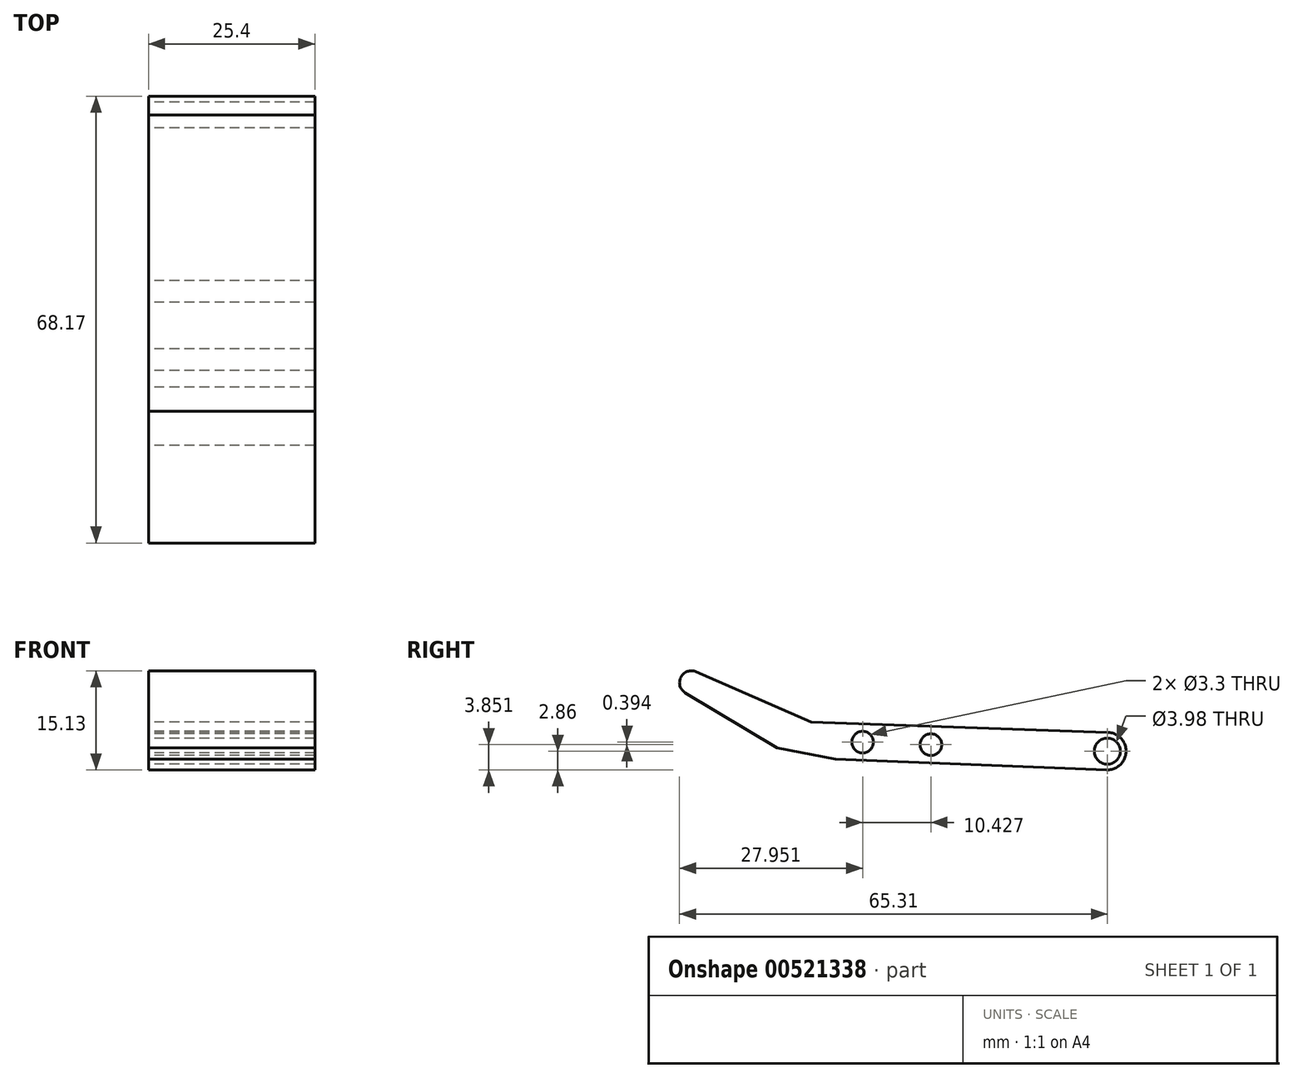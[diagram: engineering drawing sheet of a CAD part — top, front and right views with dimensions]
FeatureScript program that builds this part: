
annotation { "Feature Type Name" : "Feature", "Feature Type Description" : "" }
export const myFeature = defineFeature(function(context is Context, id is Id, definition is map)
    precondition{}
    {
        {
            var Q0;
            Q0=qCreatedBy(makeId("Right.planeOp"),FACE);
            var sketch = newSketch(context, id + "F0", { "sketchPlane" : qUnion([Q0])});
            skCircle(sketch, "E0", {"center": v(0, 0) * mm, "radius": 1.99 * mm});
            skCircle(sketch, "E1", {"center": v(0, 0) * mm, "radius": 2.86 * mm});
            skLineSegment(sketch, "E2", {"start": v(0, 2.86) * mm, "end": v(-45.23, 4.44) * mm});
            skLineSegment(sketch, "E3", {"start": v(-45.23, 4.44) * mm, "end": v(-62.77, 12.12) * mm});
            skArc(sketch, "E4", {"start": v(-62.77, 12.12) * mm, "mid": v(-65.11, 11.29) * mm, "end": v(-64.43, 8.9) * mm});
            skLineSegment(sketch, "E5", {"start": v(-64.43, 8.9) * mm, "end": v(-50.44, 0.51) * mm});
            skLineSegment(sketch, "E6", {"start": v(-50.44, 0.51) * mm, "end": v(-41.55, -1.2) * mm});
            skLineSegment(sketch, "E7", {"start": v(-41.55, -1.2) * mm, "end": v(0, -2.86) * mm});
            skCircle(sketch, "E8", {"center": v(-37.36, 1.38) * mm, "radius": 1.65 * mm});
            skCircle(sketch, "E9", {"center": v(-26.93, 1) * mm, "radius": 1.65 * mm});
            skSolve(sketch);
        }
        {
            var Q0;
            Q0 = qSketchRegion(id + "F0", true);
            extrude(context, id + "F1", {"entities" : qUnion([Q0]), "depth" : 25.4 * mm, "offsetDistance" : 25.4 * mm});
        }
    });
